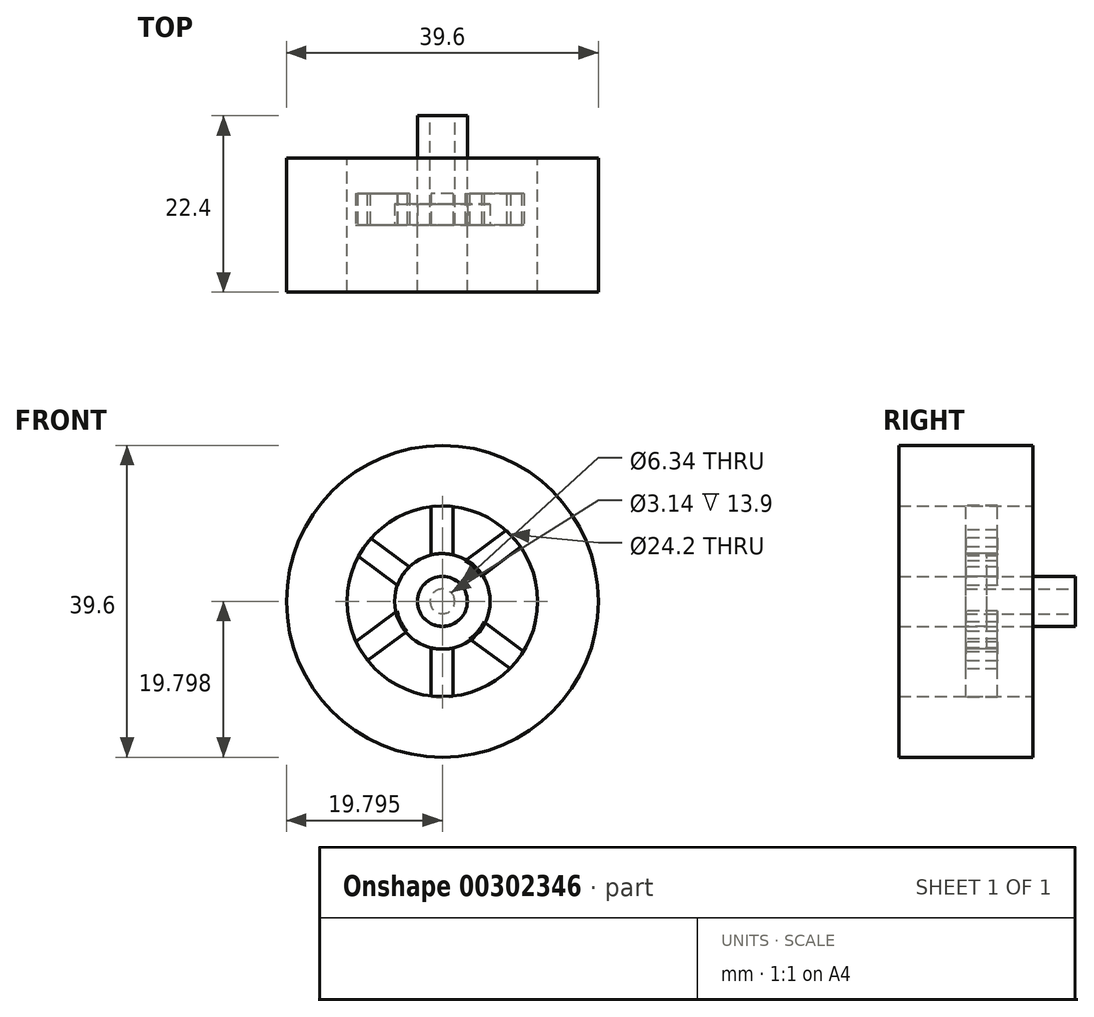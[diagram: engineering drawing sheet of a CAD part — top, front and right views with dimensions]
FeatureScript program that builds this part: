
annotation { "Feature Type Name" : "Feature", "Feature Type Description" : "" }
export const myFeature = defineFeature(function(context is Context, id is Id, definition is map)
    precondition{}
    {
        {
            var Q0;
            Q0=qCreatedBy(makeId("Front.planeOp"),FACE);
            var sketch = newSketch(context, id + "F0", { "sketchPlane" : qUnion([Q0])});
            skCircle(sketch, "E0", {"center": v(-14.5, -5.85) * mm, "radius": 3.17 * mm});
            skCircle(sketch, "E1.0", {"center": v(-14.5, -5.85) * mm, "radius": 1.57 * mm});
            skSolve(sketch);
        }
        {
            var Q0;
            Q0=makeQuery(id+"F0.imprint","IMPRINT",FACE,{"disambiguationData":[TD([[makeQuery(id+"F0.imprint","IMPRINT",EDGE,{"derivedFrom":sQuery(id+"F0.wireOp",EDGE,"E0")}),1.0]])]});
            extrude(context, id + "F1", {"entities" : qUnion([Q0]), "depth" : 9.2 * mm});
        }
        {
            var Q0;
            Q0=makeQuery(id+"F1.opExtrude","CAP_FACE",FACE,{"disambiguationData":[OSD([sQuery(id+"F0.wireOp",EDGE,"E0"),sQuery(id+"F0.wireOp",EDGE,"E1.0")])],"isStart":false});
            var sketch = newSketch(context, id + "F2", { "sketchPlane" : qUnion([Q0])});
            skCircle(sketch, "E2.0", {"center": v(-14.5, -5.85) * mm, "radius": 6.07 * mm});
            skSolve(sketch);
        }
        {
            var Q0;
            Q0=makeQuery(id+"F2.imprint","IMPRINT",FACE,{"disambiguationData":[TD([[makeQuery(id+"F2.imprint","IMPRINT",EDGE,{"derivedFrom":sQuery(id+"F2.wireOp",EDGE,"E2.0")}),1.0]])]});
            extrude(context, id + "F3", {"entities" : qUnion([Q0]), "oppositeDirection" : true, "depth" : 2.7 * mm});
        }
        {
            var Q0;
            Q0=makeQuery(id+"F3.opExtrude","CAP_FACE",FACE,{"disambiguationData":[OSD([sQuery(id+"F0.wireOp",EDGE,"E0"),sQuery(id+"F2.wireOp",EDGE,"E2.0")])],"isStart":true});
            var sketch = newSketch(context, id + "F4", { "sketchPlane" : qUnion([Q0])});
            skArc(sketch, "E3", {"start": v(-23.66, 2.2) * mm, "mid": v(-24.53, 1.09) * mm, "end": v(-25.26, -0.1) * mm});
            skLineSegment(sketch, "E4", {"start": v(-24.08, -13.4) * mm, "end": v(-19, -9.65) * mm});
            skLineSegment(sketch, "E5.0", {"start": v(-13.15, -18.05) * mm, "end": v(-13.15, -11.58) * mm});
            skLineSegment(sketch, "E6.0", {"start": v(-15.95, -18.05) * mm, "end": v(-15.95, -11.55) * mm});
            skLineSegment(sketch, "E7.0", {"start": v(-4.11, -12.26) * mm, "end": v(-9.23, -8.47) * mm});
            skLineSegment(sketch, "E8.0", {"start": v(-5.85, -14.46) * mm, "end": v(-11.04, -10.62) * mm});
            skLineSegment(sketch, "E9.0", {"start": v(-25.55, -11.01) * mm, "end": v(-20.25, -7.1) * mm});
            skLineSegment(sketch, "E10.trimOffspring", {"start": v(-13.15, -0.13) * mm, "end": v(-13.15, 6.35) * mm});
            skLineSegment(sketch, "E11.trimOffspring", {"start": v(-11.62, -0.72) * mm, "end": v(-6.32, 3.2) * mm});
            skLineSegment(sketch, "E12.trimOffspring", {"start": v(-18.55, -1.59) * mm, "end": v(-23.7, 2.22) * mm});
            skCircle(sketch, "E13", {"center": v(-14.5, -5.85) * mm, "radius": 5.88 * mm});
            skLineSegment(sketch, "E14.trimOffspring", {"start": v(-15.95, -0.15) * mm, "end": v(-15.95, 6.35) * mm});
            skLineSegment(sketch, "E15.trimOffspring", {"start": v(-20.06, -3.95) * mm, "end": v(-25.36, -0.03) * mm});
            skLineSegment(sketch, "E16.trimOffspring", {"start": v(-9.55, -2.67) * mm, "end": v(-4.46, 1.1) * mm});
            skArc(sketch, "E17.trimOffspring", {"start": v(-13.15, 6.27) * mm, "mid": v(-14.55, 6.35) * mm, "end": v(-15.95, 6.26) * mm});
            skArc(sketch, "E18.trimOffspring", {"start": v(-4.46, 1.1) * mm, "mid": v(-5.33, 2.2) * mm, "end": v(-6.32, 3.2) * mm});
            skArc(sketch, "E19.trimOffspring", {"start": v(-5.85, -14.46) * mm, "mid": v(-4.92, -13.4) * mm, "end": v(-4.11, -12.26) * mm});
            skArc(sketch, "E20.trimOffspring", {"start": v(-15.95, -17.97) * mm, "mid": v(-14.55, -18.05) * mm, "end": v(-13.15, -17.98) * mm});
            skArc(sketch, "E21.trimOffspring", {"start": v(-25.55, -11.01) * mm, "mid": v(-24.88, -12.25) * mm, "end": v(-24.08, -13.4) * mm});
            skSolve(sketch);
        }
        {
            var Q0;
            {var subQ0=sQuery(id+"F4.wireOp",EDGE,"E17.trimOffspring");Q0=makeQuery(id+"F4.imprint","IMPRINT",FACE,{"disambiguationData":[TD([[makeQuery(id+"F4.imprint","IMPRINT",EDGE,{"derivedFrom":subQ0}),1.0]])]});}
            var Q1;
            {var subQ2=sQuery(id+"F4.wireOp",EDGE,"E11.trimOffspring");Q1=makeQuery(id+"F4.imprint","IMPRINT",FACE,{"disambiguationData":[TD([[makeQuery(id+"F4.imprint","IMPRINT",EDGE,{"derivedFrom":subQ2}),-1.0]])]});}
            var Q2;
            {var subQ2=sQuery(id+"F4.wireOp",EDGE,"E7.0");Q2=makeQuery(id+"F4.imprint","IMPRINT",FACE,{"disambiguationData":[TD([[makeQuery(id+"F4.imprint","IMPRINT",EDGE,{"derivedFrom":subQ2}),1.0]])]});}
            var Q3;
            {var subQ0=sQuery(id+"F4.wireOp",EDGE,"E20.trimOffspring");Q3=makeQuery(id+"F4.imprint","IMPRINT",FACE,{"disambiguationData":[TD([[makeQuery(id+"F4.imprint","IMPRINT",EDGE,{"derivedFrom":subQ0}),1.0]])]});}
            var Q4;
            {var subQ3=sQuery(id+"F4.wireOp",EDGE,"E3");Q4=makeQuery(id+"F4.imprint","IMPRINT",FACE,{"disambiguationData":[TD([[makeQuery(id+"F4.imprint","IMPRINT",EDGE,{"derivedFrom":subQ3}),1.0]])]});}
            var Q5;
            {var subQ2=sQuery(id+"F4.wireOp",EDGE,"E4");Q5=makeQuery(id+"F4.imprint","IMPRINT",FACE,{"disambiguationData":[TD([[makeQuery(id+"F4.imprint","IMPRINT",EDGE,{"derivedFrom":subQ2}),1.0]])]});}
            extrude(context, id + "F5", {"entities" : qUnion([Q0, Q1, Q2, Q3, Q4, Q5]), "oppositeDirection" : true, "depth" : 4 * mm});
        }
        {
            var Q0;
            Q0=makeQuery(id+"F1.opExtrude","CAP_FACE",FACE,{"disambiguationData":[OSD([sQuery(id+"F0.wireOp",EDGE,"E0"),sQuery(id+"F0.wireOp",EDGE,"E1.0")])],"isStart":false});
            var sketch = newSketch(context, id + "F6", { "sketchPlane" : qUnion([Q0])});
            skCircle(sketch, "E22", {"center": v(-14.5, -5.85) * mm, "radius": 12.1 * mm});
            skCircle(sketch, "E23.0", {"center": v(-14.5, -5.85) * mm, "radius": 19.8 * mm});
            skSolve(sketch);
        }
        {
            var Q0;
            Q0=makeQuery(id+"F6.imprint","IMPRINT",FACE,{"disambiguationData":[TD([[makeQuery(id+"F6.imprint","IMPRINT",EDGE,{"derivedFrom":sQuery(id+"F6.wireOp",EDGE,"E22")}),-1.0]])]});
            extrude(context, id + "F7", {"entities" : qUnion([Q0]), "depth" : 17 * mm, "symmetric" : true});
        }
        {
            var Q0;
            Q0=makeQuery(id+"F1.opExtrude","CAP_FACE",FACE,{"disambiguationData":[OSD([sQuery(id+"F0.wireOp",EDGE,"E0"),sQuery(id+"F0.wireOp",EDGE,"E1.0")])],"isStart":true});
            extrude(context, id + "F8", {"entities" : qUnion([Q0]), "operationType" : NewBodyOperationType.ADD, "depth" : 4.7 * mm});
        }
        {
            var Q0;
            Q0=makeQuery(id+"F1.opExtrude","CAP_FACE",FACE,{"disambiguationData":[OSD([sQuery(id+"F0.wireOp",EDGE,"E0"),sQuery(id+"F0.wireOp",EDGE,"E1.0")])],"isStart":false});
            var sketch = newSketch(context, id + "F9", { "sketchPlane" : qUnion([Q0])});
            skCircle(sketch, "E24", {"center": v(-14.5, -5.85) * mm, "radius": 3.16 * mm});
            skSolve(sketch);
        }
        {
            var Q0;
            Q0=qSketchRegion(id+"F9",true);
            var Q1;
            Q1=makeQuery(id+"F7.opExtrude","CAP_FACE",FACE,{"disambiguationData":[OSD([sQuery(id+"F6.wireOp",EDGE,"E22"),sQuery(id+"F6.wireOp",EDGE,"E23.0")])],"isStart":false});
            extrude(context, id + "F10", {"entities" : qUnion([Q0]), "operationType" : NewBodyOperationType.ADD, "endBound" : BoundingType.UP_TO_SURFACE, "endBoundEntityFace" : qUnion([Q1]), "depth" : 25 * mm});
        }
        {
            var Q0;
            Q0=makeQuery(id+"F10.opExtrude","CAP_FACE",FACE,{"disambiguationData":[OSD([sQuery(id+"F9.wireOp",EDGE,"E24")])],"isStart":false});
            extrude(context, id + "F11", {"entities" : qUnion([Q0]), "operationType" : NewBodyOperationType.ADD, "oppositeDirection" : true, "depth" : 3 * mm});
        }
    });
